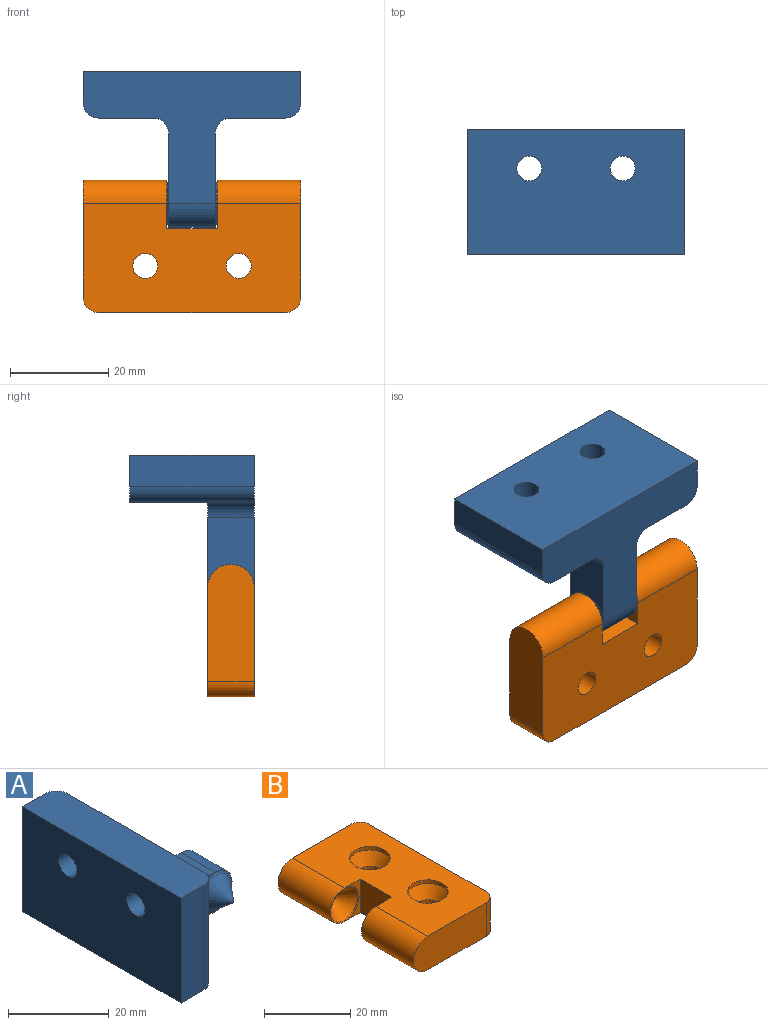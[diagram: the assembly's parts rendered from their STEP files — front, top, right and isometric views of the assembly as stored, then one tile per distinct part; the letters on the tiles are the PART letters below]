
ASSEMBLY  parts=2 mates=1
PART A: 26 faces, bbox 32.8x44.5x26.4 mm
  f0: plane 17.46x15.88mm, normal (0,0,1), area 170.7mm2, adj f1,f2,f3,f6,f22,f23
  f1: plane 14.29x9.53mm, normal (0,1,0), area 100.5mm2, adj f0,f5,f21,f22
  f2: plane 14.29x9.53mm, normal (0,-1,0), area 100.5mm2, adj f0,f5,f16,f23
  f3: cylinder r=4.76mm len=9.53mm, axis (0,-1,0), area 142.5mm2, adj f0,f5,f16,f21
  f4: plane 44.45x25.4mm, normal (-1,0,0), area 1088.5mm2, adj f5,f7,f8,f9,f10,f13
  f5: plane 44.45x26.99mm, normal (0,0,-1), area 589.7mm2, adj f1,f2,f3,f4,f6,f8,f9,f22
  f6: plane 38.1x25.4mm, normal (1,0,0), area 677.8mm2, adj f0,f5,f7,f12,f15,f22,f23,f24
  f7: plane 44.45x9.53mm, normal (0,0,1), area 419.1mm2, adj f4,f6,f8,f9,f24,f25
  f8: plane 25.4x6.35mm, normal (0,-1,0), area 161.3mm2, adj f4,f5,f7,f25
  f9: plane 25.4x6.35mm, normal (0,1,0), area 161.3mm2, adj f4,f5,f7,f24
  f10: cylinder r=2.54mm len=5.43mm, axis (1,0,0), area 86.6mm2, adj f4,f11
  f11: cone r=4.7mm half-angle=35deg, axis (1,0,0), area 85.6mm2, adj f10,f12
  f12: cylinder r=4.7mm len=9.4mm, axis (1,0,0), area 30mm2, adj f6,f11
  f13: cylinder r=2.54mm len=5.43mm, axis (1,0,0), area 86.6mm2, adj f4,f14
  f14: cone r=4.7mm half-angle=35deg, axis (1,0,0), area 85.6mm2, adj f13,f15
  f15: cylinder r=4.7mm len=9.4mm, axis (1,0,0), area 30mm2, adj f6,f14
  f16: torus R=4.76mm, axis (0,1,0), area 19.3mm2, adj f2,f3,f17
  f17: cone r=4.15mm half-angle=40deg, axis (0,1,0), area 83.9mm2, adj f16,f18
  f18: sphere r=0.4mm, area 0.4mm2, adj f17
  f19: sphere r=0.4mm, area 0.4mm2, adj f20
  f20: cone r=4.15mm half-angle=40deg, axis (0,-1,0), area 83.9mm2, adj f19,f21
  f21: torus R=4.76mm, axis (0,1,0), area 19.3mm2, adj f1,f3,f20
  f22: cylinder r=3.17mm len=9.53mm, axis (0,0,1), area 47.5mm2, adj f0,f1,f5,f6
  f23: cylinder r=3.17mm len=9.53mm, axis (0,0,-1), area 47.5mm2, adj f0,f2,f5,f6
  f24: cylinder r=3.17mm len=25.4mm, axis (0,0,1), area 126.7mm2, adj f5,f6,f7,f9
  f25: cylinder r=3.17mm len=25.4mm, axis (0,0,-1), area 126.7mm2, adj f5,f6,f7,f8
PART B: 24 faces, bbox 27.7x44.5x10.9 mm
  f0: cylinder r=4.76mm len=17.07mm, axis (0,1,0), area 255.3mm2, adj f1,f2,f6,f18
  f1: plane 44.45x22.23mm, normal (0,0,-1), area 889.8mm2, adj f0,f3,f4,f5,f6,f7,f8,f9
  f2: plane 44.45x22.23mm, normal (0,0,1), area 791.6mm2, adj f0,f3,f4,f5,f6,f7,f8,f9
  f3: cylinder r=4.76mm len=17.07mm, axis (0,1,0), area 255.3mm2, adj f1,f2,f5,f19
  f4: plane 38.1x9.53mm, normal (1,0,0), area 362.9mm2, adj f1,f2,f22,f23
  f5: plane 23.81x9.53mm, normal (0,-1,0), area 217.1mm2, adj f1,f2,f3,f23
  f6: plane 23.81x9.53mm, normal (0,1,0), area 217.1mm2, adj f0,f1,f2,f22
  f7: plane 10.32x9.53mm, normal (-1,0,0), area 98.3mm2, adj f1,f2,f8,f9
  f8: plane 9.53x5.16mm, normal (0,1,0), area 13.5mm2, adj f1,f2,f7,f19
  f9: plane 9.53x5.16mm, normal (0,-1,0), area 13.5mm2, adj f1,f2,f7,f18
  f10: cylinder r=2.54mm len=5.43mm, axis (0,0,1), area 86.6mm2, adj f1,f11
  f11: cone r=4.7mm half-angle=35deg, axis (0,0,1), area 85.6mm2, adj f10,f12
  f12: cylinder r=4.7mm len=9.4mm, axis (0,0,1), area 30mm2, adj f2,f11
  f13: cylinder r=2.54mm len=5.43mm, axis (0,0,1), area 86.6mm2, adj f1,f14
  f14: cone r=4.7mm half-angle=35deg, axis (0,0,1), area 85.6mm2, adj f13,f15
  f15: cylinder r=4.7mm len=9.4mm, axis (0,0,1), area 30mm2, adj f2,f14
  f16: sphere r=0.79mm, area 1.4mm2, adj f17
  f17: cone r=4.46mm half-angle=40deg, axis (0,-1,0), area 95.3mm2, adj f16,f18
  f18: torus R=4.76mm, axis (0,-1,0), area 10mm2, adj f0,f9,f17
  f19: torus R=4.76mm, axis (0,-1,0), area 10mm2, adj f3,f8,f20
  f20: cone r=4.46mm half-angle=40deg, axis (0,1,0), area 95.3mm2, adj f19,f21
  f21: sphere r=0.79mm, area 1.4mm2, adj f20
  f22: cylinder r=3.17mm len=9.53mm, axis (0,0,1), area 47.5mm2, adj f1,f2,f4,f6
  f23: cylinder r=3.17mm len=9.53mm, axis (0,0,-1), area 47.5mm2, adj f1,f2,f4,f5
PLACE A rot(axis=(-0.58,0.58,0.58),120deg) t=(0,-7.76,-26.99)mm
PLACE B rot(axis=(-0.58,0.58,0.58),120deg) t=(0,-7.76,-26.99)mm
MATE revolute B.f0 <-> A.f16  axis (1,0,0) through (-5.16,-7.76,-26.99)mm
